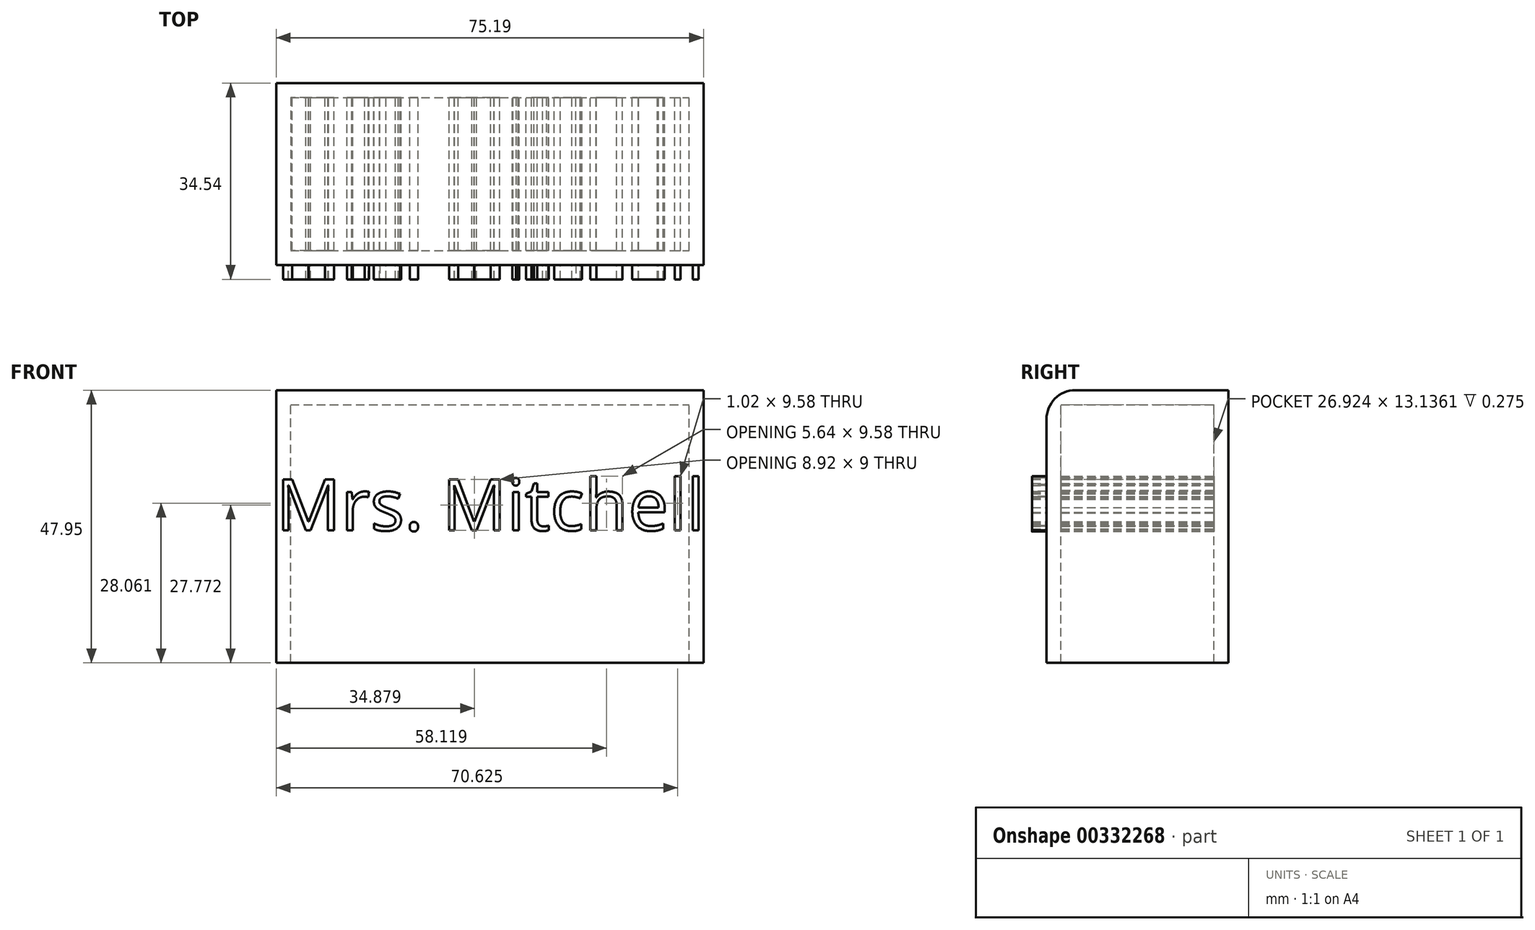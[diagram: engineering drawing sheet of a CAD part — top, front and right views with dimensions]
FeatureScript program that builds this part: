
annotation { "Feature Type Name" : "Feature", "Feature Type Description" : "" }
export const myFeature = defineFeature(function(context is Context, id is Id, definition is map)
    precondition{}
    {
        {
            var Q0;
            Q0=qCreatedBy(makeId("Front.planeOp"),FACE);
            var sketch = newSketch(context, id + "F0", { "sketchPlane" : qUnion([Q0])});
            skLineSegment(sketch, "E0.bottom", {"start": v(-39.72, 0) * mm, "end": v(35.47, 0) * mm});
            skLineSegment(sketch, "E0.top", {"start": v(-39.72, 47.95) * mm, "end": v(35.47, 47.95) * mm});
            skLineSegment(sketch, "E0.left", {"start": v(-39.72, 0) * mm, "end": v(-39.72, 47.95) * mm});
            skLineSegment(sketch, "E0.right", {"start": v(35.47, 0) * mm, "end": v(35.47, 47.95) * mm});
            skSolve(sketch);
        }
        {
            var Q0;
            Q0=makeQuery(id+"F0.imprint","IMPRINT",FACE,{"disambiguationData":[TD([[makeQuery(id+"F0.imprint","IMPRINT",EDGE,{"derivedFrom":sQuery(id+"F0.wireOp",EDGE,"E0.bottom")}),1.0]])]});
            extrude(context, id + "F1", {"entities" : qUnion([Q0]), "depth" : 32 * mm});
        }
        {
            var Q0;
            Q0=makeQuery(id+"F1.opExtrude","SWEPT_FACE",FACE,{"disambiguationData":[OSD([sQuery(id+"F0.wireOp",EDGE,"E0.bottom")])]});
            shell(context, id + "F2", {"entities" : qUnion([Q0]), "thickness" : 2.54 * mm});
        }
        {
            var Q0;
            Q0=makeQuery(id+"F1.opExtrude","CAP_EDGE",EDGE,{"disambiguationData":[OSD([sQuery(id+"F0.wireOp",EDGE,"E0.top")])],"isStart":false});
            fillet(context, id + "F3", {"entities" : qUnion([Q0]), "radius" : 5.08 * mm, "tangentPropagation" : true, "allowEdgeOverflow" : false});
        }
        {
            var Q0;
            Q0=qCreatedBy(makeId("Front.planeOp"),FACE);
            var sketch = newSketch(context, id + "F4", { "sketchPlane" : qUnion([Q0])});
            skText(sketch, "E1", { "text": "Mrs. Mitchell", "fontName": "OpenSans-Regular.ttf"});
            const initialGuessF4  = {"E1": [-0.03972, 0.02327, 1, 0, 0.00908]};
            skSetInitialGuess(sketch, initialGuessF4);
            skSolve(sketch);
        }
        {
            var Q0;
            Q0 = qSketchRegion(id + "F4", true);
            extrude(context, id + "F5", {"entities" : qUnion([Q0]), "operationType" : NewBodyOperationType.ADD, "depth" : 34.54 * mm});
        }
    });
